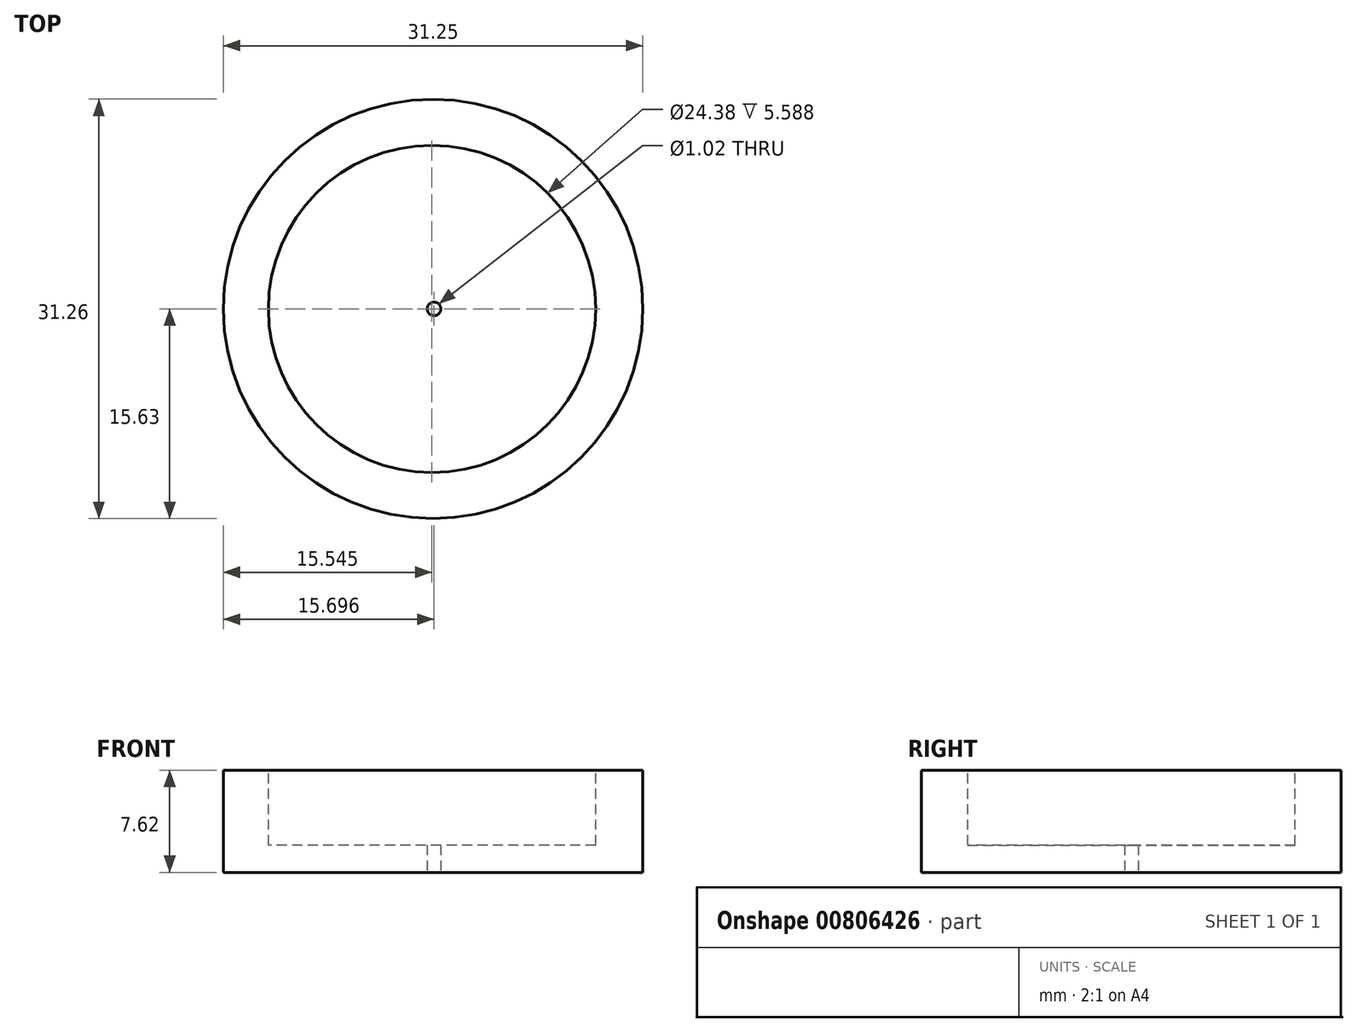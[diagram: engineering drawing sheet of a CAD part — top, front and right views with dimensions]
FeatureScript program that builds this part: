
annotation { "Feature Type Name" : "Feature", "Feature Type Description" : "" }
export const myFeature = defineFeature(function(context is Context, id is Id, definition is map)
    precondition{}
    {
        {
            var Q0;
            Q0=qCreatedBy(makeId("Top.planeOp"),FACE);
            var sketch = newSketch(context, id + "F0", { "sketchPlane" : qUnion([Q0])});
            skCircle(sketch, "E0", {"center": v(-47.42, 29.7) * mm, "radius": 15.63 * mm});
            skPoint(sketch, "E0.first.point", {"position": v(-56.53, 42.4) * mm});
            skPoint(sketch, "E0.second.point", {"position": v(-32.87, 24) * mm});
            skPoint(sketch, "E0.third.point", {"position": v(-57.25, 17.56) * mm});
            skSolve(sketch);
        }
        {
            var Q0;
            Q0 = qSketchRegion(id + "F0", true);
            extrude(context, id + "F1", {"entities" : qUnion([Q0]), "depth" : 7.62 * mm, "offsetDistance" : 25.4 * mm});
        }
        {
            var Q0;
            Q0=qCreatedBy(makeId("Top.planeOp"),FACE);
            var sketch = newSketch(context, id + "F2", { "sketchPlane" : qUnion([Q0])});
            skCircle(sketch, "E1", {"center": v(-47.5, 29.7) * mm, "radius": 12.2 * mm});
            skPoint(sketch, "E1.first.point", {"position": v(-55.42, 38.98) * mm});
            skPoint(sketch, "E1.second.point", {"position": v(-35.66, 26.84) * mm});
            skPoint(sketch, "E1.third.point", {"position": v(-50.22, 17.82) * mm});
            skSolve(sketch);
        }
        {
            var Q0;
            Q0 = qSketchRegion(id + "F2", true);
            extrude(context, id + "F3", {"entities" : qUnion([Q0]), "operationType" : NewBodyOperationType.ADD, "depth" : 25.4 * mm, "offsetDistance" : 25.4 * mm});
        }
        {
            var Q0;
            Q0=makeQuery(id+"F3.opExtrude","CAP_FACE",FACE,{"disambiguationData":[OSD([sQuery(id+"F2.wireOp",EDGE,"E1")])],"isStart":false});
            extrude(context, id + "F4", {"entities" : qUnion([Q0]), "operationType" : NewBodyOperationType.REMOVE, "endBound" : BoundingType.SYMMETRIC, "oppositeDirection" : true, "depth" : 46.74 * mm, "offsetDistance" : 25.4 * mm});
        }
        {
            var Q0;
            Q0=qCreatedBy(makeId("Top.planeOp"),FACE);
            var sketch = newSketch(context, id + "F5", { "sketchPlane" : qUnion([Q0])});
            skCircle(sketch, "E2", {"center": v(-47.35, 29.7) * mm, "radius": 0.5 * mm});
            skPoint(sketch, "E2.first.point", {"position": v(-47.8, 29.94) * mm});
            skPoint(sketch, "E2.second.point", {"position": v(-47.06, 29.3) * mm});
            skPoint(sketch, "E2.third.point", {"position": v(-46.89, 29.51) * mm});
            skSolve(sketch);
        }
        {
            var Q0;
            Q0 = qSketchRegion(id + "F5", true);
            extrude(context, id + "F6", {"entities" : qUnion([Q0]), "operationType" : NewBodyOperationType.REMOVE, "endBound" : BoundingType.SYMMETRIC, "depth" : 25.4 * mm, "offsetDistance" : 25.4 * mm});
        }
    });
